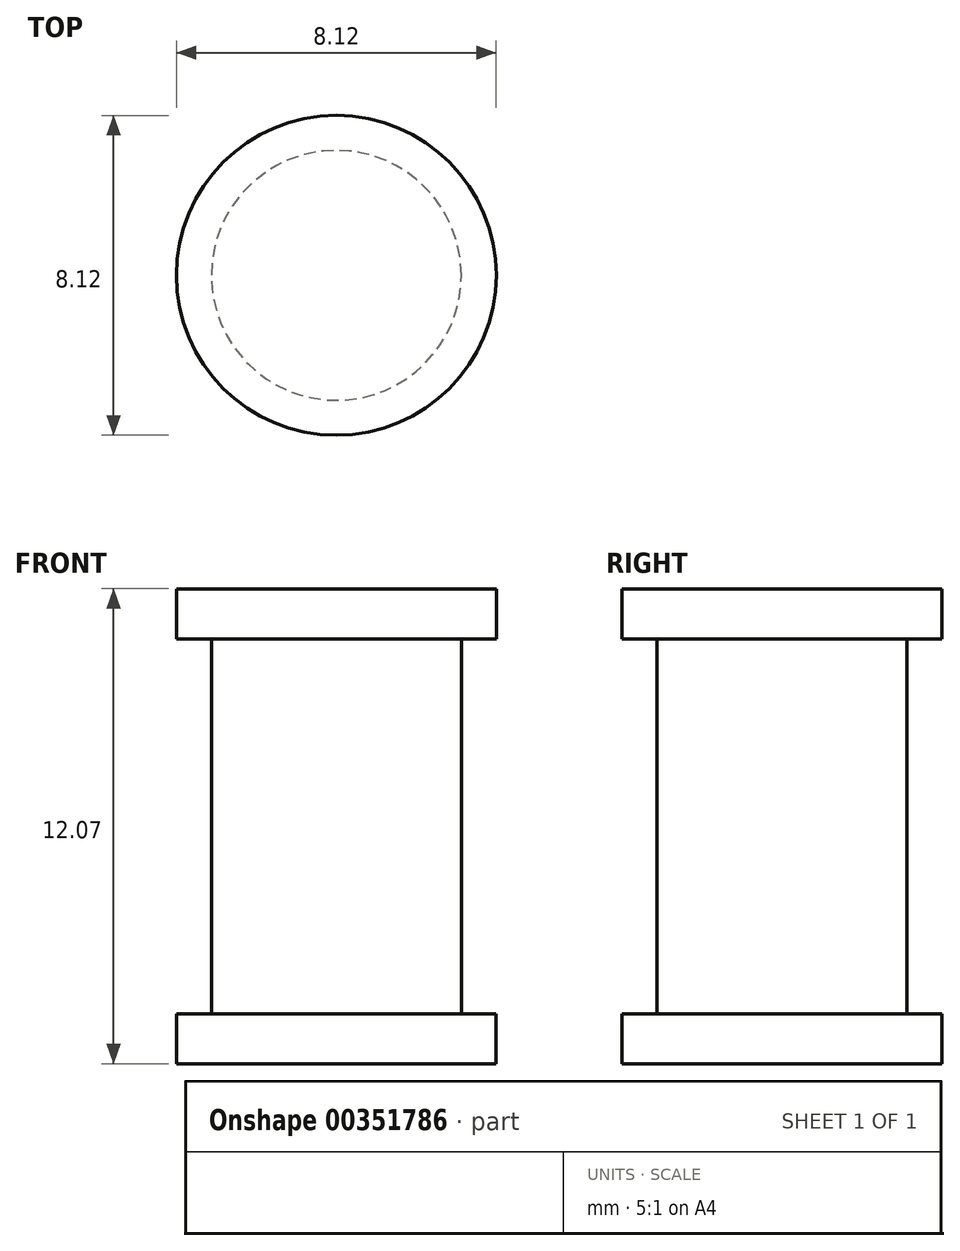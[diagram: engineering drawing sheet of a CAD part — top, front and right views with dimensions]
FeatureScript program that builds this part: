
annotation { "Feature Type Name" : "Feature", "Feature Type Description" : "" }
export const myFeature = defineFeature(function(context is Context, id is Id, definition is map)
    precondition{}
    {
        {
            var Q0;
            Q0=qCreatedBy(makeId("Top.planeOp"),FACE);
            var sketch = newSketch(context, id + "F0", { "sketchPlane" : qUnion([Q0])});
            skCircle(sketch, "E0", {"center": v(0, 0) * mm, "radius": 3.17 * mm});
            skSolve(sketch);
        }
        {
            var Q0;
            Q0 = qSketchRegion(id + "F0", true);
            extrude(context, id + "F1", {"entities" : qUnion([Q0]), "depth" : 9.52 * mm});
        }
        {
            var Q0;
            Q0=makeQuery(id+"F1.opExtrude","CAP_FACE",FACE,{"disambiguationData":[OSD([sQuery(id+"F0.wireOp",EDGE,"E0")])],"isStart":true});
            var sketch = newSketch(context, id + "F2", { "sketchPlane" : qUnion([Q0])});
            skCircle(sketch, "E1", {"center": v(0, 0) * mm, "radius": 4.06 * mm});
            skSolve(sketch);
        }
        {
            var Q0;
            Q0 = qSketchRegion(id + "F2", true);
            extrude(context, id + "F3", {"entities" : qUnion([Q0]), "operationType" : NewBodyOperationType.ADD, "depth" : 1.27 * mm});
        }
        {
            var Q0;
            Q0=makeQuery(id+"F1.opExtrude","CAP_FACE",FACE,{"disambiguationData":[OSD([sQuery(id+"F0.wireOp",EDGE,"E0")])],"isStart":false});
            var sketch = newSketch(context, id + "F4", { "sketchPlane" : qUnion([Q0])});
            skCircle(sketch, "E2", {"center": v(0, 0) * mm, "radius": 4.06 * mm});
            skSolve(sketch);
        }
        {
            var Q0;
            Q0 = qSketchRegion(id + "F4", true);
            extrude(context, id + "F5", {"entities" : qUnion([Q0]), "operationType" : NewBodyOperationType.ADD, "depth" : 1.27 * mm});
        }
    });
